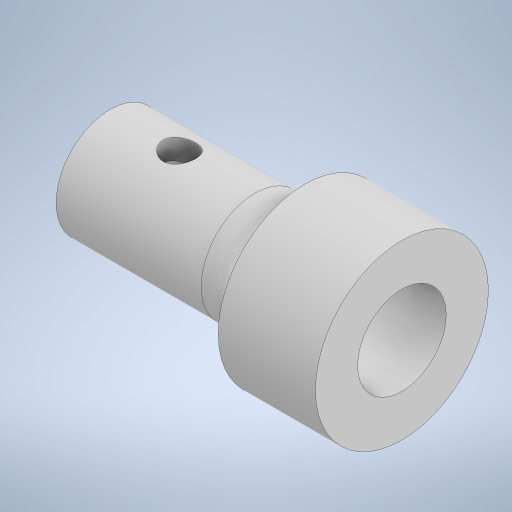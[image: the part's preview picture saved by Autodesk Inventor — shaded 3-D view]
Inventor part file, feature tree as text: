
AUTODESK INVENTOR PART (.ipt)
format: ipt  version: 2024 (Build 280153000, 153)  size: 273,408 bytes
history: native  units: in
note: dims shown in document units (in); Inventor stores cm internally (conversion verified against a paired STEP export)
features: extrude x4, sketch x4, fillet x1
ambient origin geometry x8: Origin, YZ Plane, XZ Plane, XY Plane, X Axis, Y Axis, Z Axis, Center Point
bodies: Solid1 (feature_tree)
feature tree (9):
  extrude  "Extrusion1"  Depth=0.3937in
  extrude  "Extrusion2"  Depth=0.3937in
  extrude  "Extrusion3"  Depth=0.3228in
  fillet  "Fillet1"  Radius=0.6299in
  extrude  "Extrusion4"  Depth=0.1969in
  sketch  "Sketch1"  dims[d0=0.248in d1=0.3937in]
  sketch  "Sketch2"  dims[d2=0.7087in d3=0.0in d4=0.3937in]
  sketch  "Sketch3"  dims[d5=0.0787in d6=0.0in d7=0.3228in d8=0.6299in]
  sketch  "Sketch4"  dims[d9=0.3543in d10=0.0in d11=0.1969in d12=0.2756in d13=0.1181in d14=1.7323in d15=0.0in]
